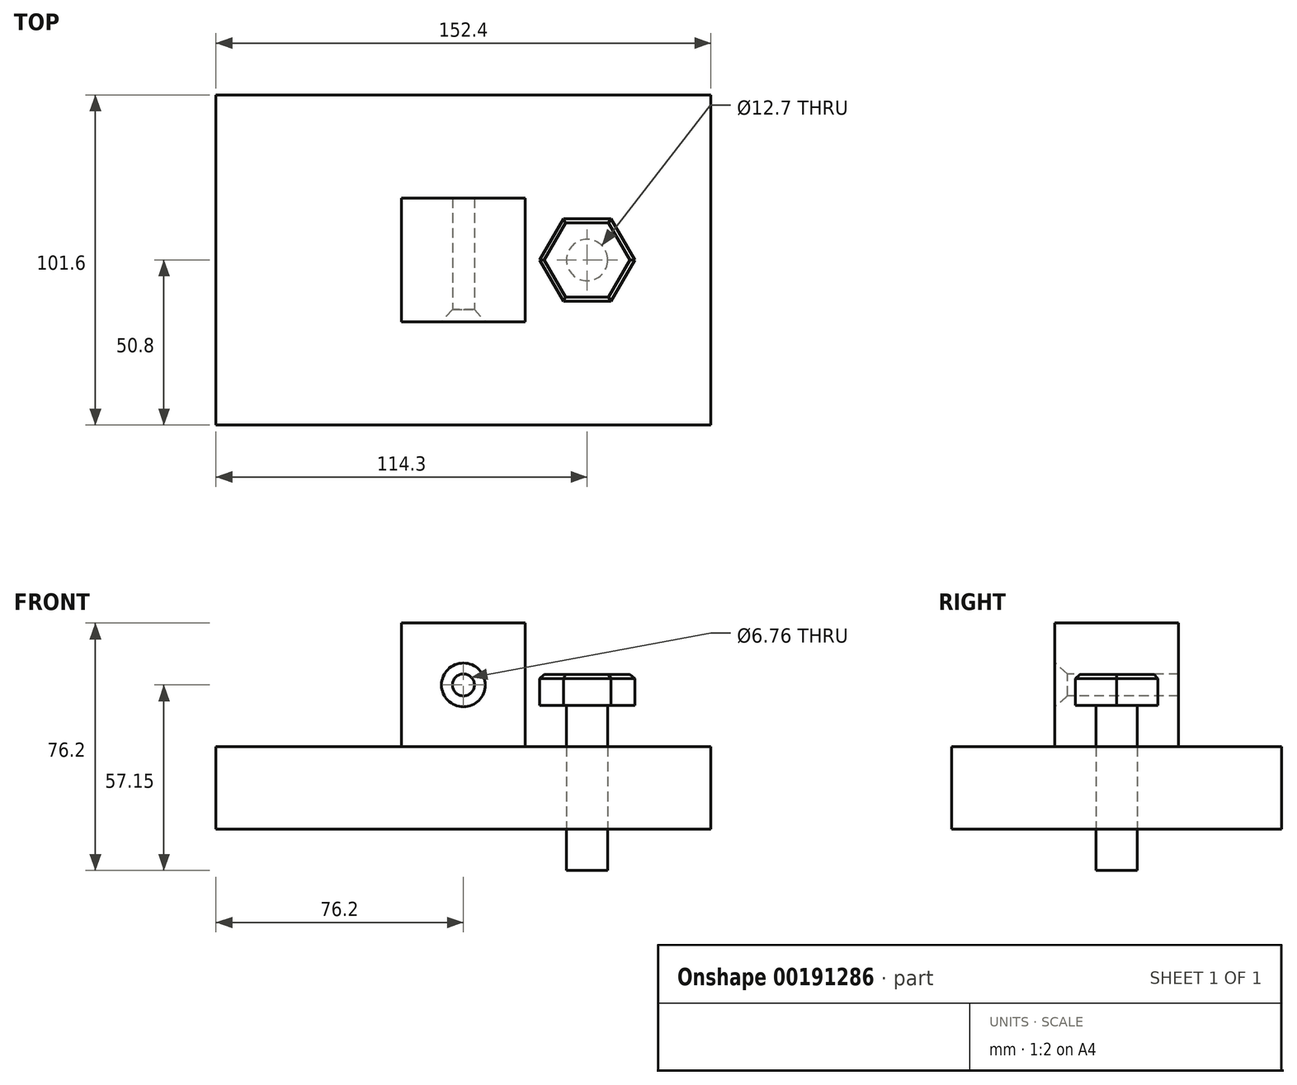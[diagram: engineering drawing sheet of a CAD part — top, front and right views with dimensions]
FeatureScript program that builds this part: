
annotation { "Feature Type Name" : "Feature", "Feature Type Description" : "" }
export const myFeature = defineFeature(function(context is Context, id is Id, definition is map)
    precondition{}
    {
        {
            var Q0;
            Q0=qCreatedBy(makeId("Top.planeOp"),FACE);
            var sketch = newSketch(context, id + "F0", { "sketchPlane" : qUnion([Q0])});
            skLineSegment(sketch, "E0.bottom", {"start": v(76.2, -50.8) * mm, "end": v(-76.2, -50.8) * mm});
            skLineSegment(sketch, "E0.top", {"start": v(76.2, 50.8) * mm, "end": v(-76.2, 50.8) * mm});
            skLineSegment(sketch, "E0.left", {"start": v(76.2, -50.8) * mm, "end": v(76.2, 50.8) * mm});
            skLineSegment(sketch, "E0.right", {"start": v(-76.2, -50.8) * mm, "end": v(-76.2, 50.8) * mm});
            skPoint(sketch, "E0.middle", {"position": v(0, 0) * mm});
            skLineSegment(sketch, "E1", {"start": v(0, 0) * mm, "end": v(76.2, 0) * mm, "construction": true});
            skCircle(sketch, "E2", {"center": v(38.1, 0) * mm, "radius": 6.35 * mm});
            skCircle(sketch, "E3.cCircle", {"center": v(38.1, 0) * mm, "radius": 12.7 * mm, "construction": true});
            skLineSegment(sketch, "E3.0", {"start": v(52.76, 0) * mm, "end": v(45.43, -12.7) * mm});
            skLineSegment(sketch, "E3.1", {"start": v(45.43, -12.7) * mm, "end": v(30.77, -12.7) * mm});
            skLineSegment(sketch, "E3.2", {"start": v(30.77, -12.7) * mm, "end": v(23.44, 0) * mm});
            skLineSegment(sketch, "E3.3", {"start": v(23.44, 0) * mm, "end": v(30.77, 12.7) * mm});
            skLineSegment(sketch, "E3.4", {"start": v(30.77, 12.7) * mm, "end": v(45.43, 12.7) * mm});
            skLineSegment(sketch, "E3.5", {"start": v(45.43, 12.7) * mm, "end": v(52.76, 0) * mm});
            skPoint(sketch, "E3.0.midPoint", {"position": v(49.1, -6.35) * mm});
            skSolve(sketch);
        }
        {
            var Q0;
            Q0=makeQuery(id+"F0.imprint","IMPRINT",FACE,{"disambiguationData":[TD([[makeQuery(id+"F0.imprint","IMPRINT",EDGE,{"derivedFrom":sQuery(id+"F0.wireOp",EDGE,"E0.bottom")}),-1.0]])]});
            var Q1;
            Q1=makeQuery(id+"F0.imprint","IMPRINT",FACE,{"disambiguationData":[TD([[makeQuery(id+"F0.imprint","IMPRINT",EDGE,{"derivedFrom":sQuery(id+"F0.wireOp",EDGE,"E2")}),-1.0]])]});
            extrude(context, id + "F1", {"entities" : qUnion([Q0, Q1]), "endBound" : BoundingType.SYMMETRIC, "depth" : 25.4 * mm});
        }
        {
            var Q0;
            Q0=makeQuery(id+"F1.opExtrude","CAP_FACE",FACE,{"disambiguationData":[OSD([sQuery(id+"F0.wireOp",EDGE,"E0.bottom"),sQuery(id+"F0.wireOp",EDGE,"E0.top"),sQuery(id+"F0.wireOp",EDGE,"E0.left"),sQuery(id+"F0.wireOp",EDGE,"E0.right")])],"isStart":false});
            var sketch = newSketch(context, id + "F2", { "sketchPlane" : qUnion([Q0])});
            skLineSegment(sketch, "E4.bottom", {"start": v(19.05, -19.05) * mm, "end": v(-19.05, -19.05) * mm});
            skLineSegment(sketch, "E4.top", {"start": v(19.05, 19.05) * mm, "end": v(-19.05, 19.05) * mm});
            skLineSegment(sketch, "E4.left", {"start": v(19.05, -19.05) * mm, "end": v(19.05, 19.05) * mm});
            skLineSegment(sketch, "E4.right", {"start": v(-19.05, -19.05) * mm, "end": v(-19.05, 19.05) * mm});
            skPoint(sketch, "E4.middle", {"position": v(0, 0) * mm});
            skSolve(sketch);
        }
        {
            var Q0;
            Q0=qSketchRegion(id+"F2",true);
            extrude(context, id + "F3", {"entities" : qUnion([Q0]), "depth" : 38.1 * mm});
        }
        {
            var Q0;
            Q0=makeQuery(id+"F0.imprint","IMPRINT",FACE,{"disambiguationData":[TD([[makeQuery(id+"F0.imprint","IMPRINT",EDGE,{"derivedFrom":sQuery(id+"F0.wireOp",EDGE,"E2")}),1.0]])]});
            extrude(context, id + "F4", {"entities" : qUnion([Q0]), "endBound" : BoundingType.SYMMETRIC, "depth" : 50.8 * mm});
        }
        {
            var Q0;
            Q0=makeQuery(id+"F4.opExtrude","CAP_FACE",FACE,{"disambiguationData":[OSD([sQuery(id+"F0.wireOp",EDGE,"E2")])],"isStart":false});
            var sketch = newSketch(context, id + "F5", { "sketchPlane" : qUnion([Q0])});
            skSolve(sketch);
        }
        {
            var Q0;
            Q0=makeQuery(id+"F5.imprint","IMPRINT",FACE,{"disambiguationData":[TD([[makeQuery(id+"F5.imprint","IMPRINT",EDGE,{"derivedFrom":makeQuery(id+"F4.opExtrude","CAP_EDGE",EDGE,{"disambiguationData":[OSD([sQuery(id+"F0.wireOp",EDGE,"E2")])],"isStart":false})}),1.0]])]});
            var sketch = newSketch(context, id + "F6", { "sketchPlane" : qUnion([Q0])});
            skLineSegment(sketch, "E5.0", {"start": v(45.43, -12.7) * mm, "end": v(30.77, -12.7) * mm});
            skLineSegment(sketch, "E5.1", {"start": v(52.76, 0) * mm, "end": v(45.43, -12.7) * mm});
            skLineSegment(sketch, "E5.2", {"start": v(45.43, 12.7) * mm, "end": v(52.76, 0) * mm});
            skLineSegment(sketch, "E5.3", {"start": v(30.77, 12.7) * mm, "end": v(45.43, 12.7) * mm});
            skLineSegment(sketch, "E5.4", {"start": v(23.44, 0) * mm, "end": v(30.77, 12.7) * mm});
            skLineSegment(sketch, "E5.5", {"start": v(30.77, -12.7) * mm, "end": v(23.44, 0) * mm});
            skSolve(sketch);
        }
        {
            var Q0;
            Q0=qSketchRegion(id+"F6",true);
            extrude(context, id + "F7", {"entities" : qUnion([Q0]), "operationType" : NewBodyOperationType.ADD, "depth" : 9.52 * mm});
        }
        {
            var Q0;
            Q0=makeQuery(id+"F7.opExtrude","CAP_FACE",FACE,{"disambiguationData":[OSD([sQuery(id+"F6.wireOp",EDGE,"E5.0"),sQuery(id+"F6.wireOp",EDGE,"E5.1"),sQuery(id+"F6.wireOp",EDGE,"E5.2"),sQuery(id+"F6.wireOp",EDGE,"E5.3"),sQuery(id+"F6.wireOp",EDGE,"E5.4"),sQuery(id+"F6.wireOp",EDGE,"E5.5")])],"isStart":false});
            chamfer(context, id + "F8", {"entities" : qUnion([Q0]), "width" : 1.27 * mm, "tangentPropagation" : true});
        }
        {
            var Q0;
            Q0=makeQuery(id+"F3.opExtrude","SWEPT_FACE",FACE,{"disambiguationData":[OSD([sQuery(id+"F2.wireOp",EDGE,"E4.bottom")])]});
            var sketch = newSketch(context, id + "F9", { "sketchPlane" : qUnion([Q0])});
            skPoint(sketch, "E6", {"position": v(0, 31.75) * mm});
            skPoint(sketch, "E6.positionSnap0", {"position": v(-19.05, 31.75) * mm});
            skSolve(sketch);
        }
        {
            var Q0;
            Q0=sQuery(id+"F9.wireOp",VERTEX,"E6");
            var Q1;
            Q1=makeQuery(id+"F3.opExtrude","SWEPT_BODY",BODY,{"disambiguationData":[OSD([sQuery(id+"F2.wireOp",EDGE,"E4.bottom"),sQuery(id+"F2.wireOp",EDGE,"E4.top"),sQuery(id+"F2.wireOp",EDGE,"E4.left"),sQuery(id+"F2.wireOp",EDGE,"E4.right")])]});
            hole(context, id + "F10", {"style" : HoleStyle.C_SINK, "endStyle" : HoleEndStyle.THROUGH, "standardTappedOrClearance" : lookupTablePath({ "standard" : "ANSI", "fit" : "Normal (ASME)", "size" : "1/4", "type" : "Clearance" }), "standardBlindInLast" : lookupTablePath({ "fit" : "Free", "standard" : "ANSI", "size" : "1/4", "type" : "Clearance" }), "holeDiameter" : 6.76 * mm, "cSinkDiameter" : 13.5 * mm, "cSinkAngle" : 82 * degree, "locations" : qUnion([Q0]), "scope" : qUnion([Q1]), "isTappedThrough" : true});
        }
    });
